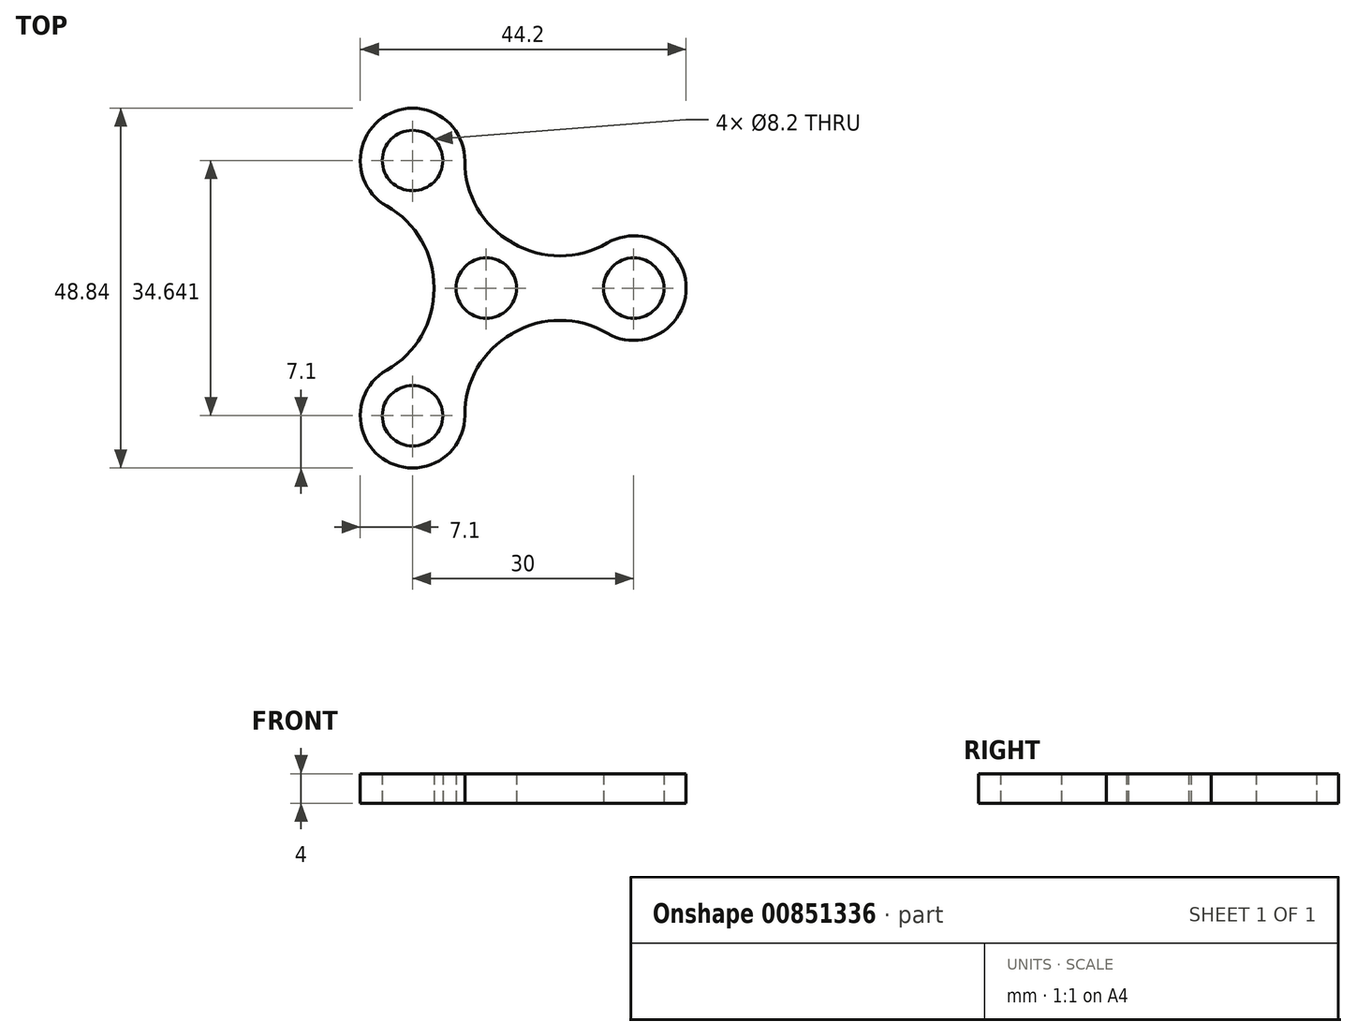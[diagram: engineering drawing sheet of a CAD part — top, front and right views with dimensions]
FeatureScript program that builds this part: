
annotation { "Feature Type Name" : "Feature", "Feature Type Description" : "" }
export const myFeature = defineFeature(function(context is Context, id is Id, definition is map)
    precondition{}
    {
        {
            var Q0;
            Q0=qCreatedBy(makeId("Top.planeOp"),FACE);
            var sketch = newSketch(context, id + "F0", { "sketchPlane" : qUnion([Q0])});
            skCircle(sketch, "E0", {"center": v(0, 0) * mm, "radius": 4.1 * mm});
            skCircle(sketch, "E1", {"center": v(0, 0) * mm, "radius": 7.1 * mm});
            skCircle(sketch, "E2", {"center": v(20, 0) * mm, "radius": 7.1 * mm});
            skLineSegment(sketch, "E3", {"start": v(0, 0) * mm, "end": v(20, 0) * mm, "construction": true});
            skLineSegment(sketch, "E4", {"start": v(10, 0) * mm, "end": v(10, 20.08) * mm, "construction": true});
            skCircle(sketch, "E5", {"center": v(20, 0) * mm, "radius": 4.1 * mm});
            skArc(sketch, "E6", {"start": v(3.6, 6.12) * mm, "mid": v(10, 4.38) * mm, "end": v(16.4, 6.12) * mm});
            skArc(sketch, "E7", {"start": v(16.4, 6.12) * mm, "mid": v(10, 29.62) * mm, "end": v(3.6, 6.12) * mm, "construction": true});
            skArc(sketch, "E8", {"start": v(3.6, -6.12) * mm, "mid": v(10, -4.38) * mm, "end": v(16.4, -6.12) * mm});
            skArc(sketch, "E9", {"start": v(16.4, -6.12) * mm, "mid": v(10, -29.62) * mm, "end": v(3.6, -6.12) * mm, "construction": true});
            skCircle(sketch, "E10.1.0", {"center": v(-10, 17.32) * mm, "radius": 7.1 * mm});
            skCircle(sketch, "E10.1.1", {"center": v(-10, 17.32) * mm, "radius": 4.1 * mm});
            skArc(sketch, "E10.1.2", {"start": v(-7.1, 0.06) * mm, "mid": v(-8.8, 6.47) * mm, "end": v(-13.5, 11.14) * mm});
            skArc(sketch, "E10.1.3", {"start": v(3.5, 6.18) * mm, "mid": v(-1.2, 10.85) * mm, "end": v(-2.9, 17.26) * mm});
            skCircle(sketch, "E10.2.0", {"center": v(-10, -17.32) * mm, "radius": 7.1 * mm});
            skCircle(sketch, "E10.2.1", {"center": v(-10, -17.32) * mm, "radius": 4.1 * mm});
            skArc(sketch, "E10.2.2", {"start": v(3.5, -6.18) * mm, "mid": v(-1.2, -10.85) * mm, "end": v(-2.9, -17.26) * mm});
            skArc(sketch, "E10.2.3", {"start": v(-7.1, -0.06) * mm, "mid": v(-8.8, -6.47) * mm, "end": v(-13.5, -11.14) * mm});
            skSolve(sketch);
        }
        {
            var Q0;
            {var subQ0=sQuery(id+"F0.wireOp",EDGE,"E10.2.2");Q0=makeQuery(id+"F0.imprint","IMPRINT",FACE,{"disambiguationData":[TD([[makeQuery(id+"F0.imprint","IMPRINT",EDGE,{"derivedFrom":subQ0}),-1.0]])]});}
            var Q1;
            Q1=makeQuery(id+"F0.imprint","IMPRINT",FACE,{"disambiguationData":[TD([[makeQuery(id+"F0.imprint","IMPRINT",EDGE,{"derivedFrom":sQuery(id+"F0.wireOp",EDGE,"E10.2.1")}),-1.0]])]});
            var Q2;
            Q2=makeQuery(id+"F0.imprint","IMPRINT",FACE,{"disambiguationData":[TD([[makeQuery(id+"F0.imprint","IMPRINT",EDGE,{"derivedFrom":sQuery(id+"F0.wireOp",EDGE,"E0")}),-1.0]])]});
            var Q3;
            {var subQ0=sQuery(id+"F0.wireOp",EDGE,"E6");Q3=makeQuery(id+"F0.imprint","IMPRINT",FACE,{"disambiguationData":[TD([[makeQuery(id+"F0.imprint","IMPRINT",EDGE,{"derivedFrom":subQ0}),-1.0]])]});}
            var Q4;
            Q4=makeQuery(id+"F0.imprint","IMPRINT",FACE,{"disambiguationData":[TD([[makeQuery(id+"F0.imprint","IMPRINT",EDGE,{"derivedFrom":sQuery(id+"F0.wireOp",EDGE,"E5")}),-1.0]])]});
            var Q5;
            {var subQ0=sQuery(id+"F0.wireOp",EDGE,"E10.1.2");Q5=makeQuery(id+"F0.imprint","IMPRINT",FACE,{"disambiguationData":[TD([[makeQuery(id+"F0.imprint","IMPRINT",EDGE,{"derivedFrom":subQ0}),-1.0]])]});}
            var Q6;
            Q6=makeQuery(id+"F0.imprint","IMPRINT",FACE,{"disambiguationData":[TD([[makeQuery(id+"F0.imprint","IMPRINT",EDGE,{"derivedFrom":sQuery(id+"F0.wireOp",EDGE,"E10.1.1")}),-1.0]])]});
            extrude(context, id + "F1", {"entities" : qUnion([Q0, Q1, Q2, Q3, Q4, Q5, Q6]), "depth" : 4 * mm, "offsetDistance" : 25 * mm});
        }
    });
